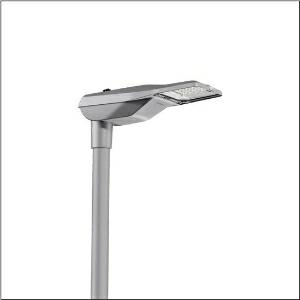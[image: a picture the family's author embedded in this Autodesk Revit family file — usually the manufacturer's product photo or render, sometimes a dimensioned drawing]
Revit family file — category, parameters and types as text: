
# Revit family: streetlight_sl_21_micro___st1_0a_5xe1d43s08db_64f0
name_source: partatom
category: Lighting Fixtures
units: mm (PartAtom-declared; Revit-internal decimal feet)

## family parameters
Cut with Voids When Loaded = No
Host = Face
Light Source = No
Part Type = Normal
Room Calculation Point = No
Round Connector Dimension = Use Diameter
Shared = No

## types (1)
- --- (1 x LED, 5320 lm, 39.1 W, 4000K)
    Apparent Load = 39 VA
    CIE Flux Codes = 37 72 97 100 100
    Color Rendering = 70
    Color Temperature = 4000K
    Default Elevation = 1800 mm
    Description = Streetlight SL 21 micro, mast luminaire, primary light control with lens, of PMMA, primary optical cover: cover, of toughened safety glass, transparent, light distribution: ST1.0a, light emission: direct distribution, primary light characteristic: asymmetric, installation type: side-entry, post-top, LED, High Power LED, rated luminous flux: 5.320lm, luminous efficacy: 136lm/W, light colour: 740, colour temperature: 4000K, control gear: D4i, control: flexible luminous flux parameterisation, time-dependent luminous flux control, constant luminous flux control, overheat protection, pre-setting: logarithmic dimming characteristic, mains connection: 220..240V, AC, 50/60Hz, start of lifetime: 39W, end of service life: 41W, reduction: 18W, luminaire housing, of diecast aluminium, powder-coated, Siteco® metallic grey (DB 702S), corrosivity category C5 mid according to DIN EN ISO 12944, please order mast flange separately, inclination adjustable: 0°, 5°, 10°, 15°, sealing non-destructively replaceable, multi-level sealing system, length: 528mm, width: 235mm, height: 110mm, mast flange for spigot size: 42mm (side-entry): 5XC10008XM4, 60/48mm (side-entry/post-top): 5XC10108XM2, 76/60mm (side-entry/post-top): 5XC10108XM1, Smart Interface above, protection rating (complete): IP66, insulation class (complete): insulation class II (safety insulation), certification: CE, ENEC, ENEC+, VDE, impact resistance: IK10, permissible operating ambient temperature for outdoor applications: -40..+50°C, standard-compliant lighting for roads and squares, packaging unit: 1 piece

Light Distribution: ST1.0a
    Height = 110 mm
    Lamp = 1 x LED
    Lamp Light Flux = 5320 lm
    Lamp Power = 39.1 W
    Lamp count = 1
    Length = 528 mm
    Luminous efficacy = 136 lm/W
    Manufacturer = Siteco
    ModVariant = No
    Model = 5XE1D43S08DB
    Number of Poles = 1
    OnlyDefault = Yes
    Power Factor = 1
    Product Name = Streetlight SL 21 micro | ST1.0a
    Product group = mast luminaire | pylon top
    ProductGroupID = 6100
    Protection Class = Protection class II
    Protection Degree = IP 66
    RLX_Detail_Level = 1
    RLX_Emergency_Light_Flux = 0 lm
    RLX_Emergency_Type = 0
    RLX_Emergency_Type_DB = No
    RlxData = <blob elided: 98445 chars, md5=b68fc024>
    Socket = socket
    Standby Power = 0 W
    System Light Flux = 5320 lm
    System Power = 39 W
    Type Comments = factory setting: luminous flux: 100 % | dim-lin: 254 | 765 mA
    Type Image = l_1277292.jpg
    URL = http://relux.com
    VarID = @adj_177277
    Voltage = 0 V
    Weight = 0.00 kg
    Width = 235 mm

## geometry (parser evidence)
native form markers: Blend x4, Sweep x11
no freeform markers — native parametric forms only
